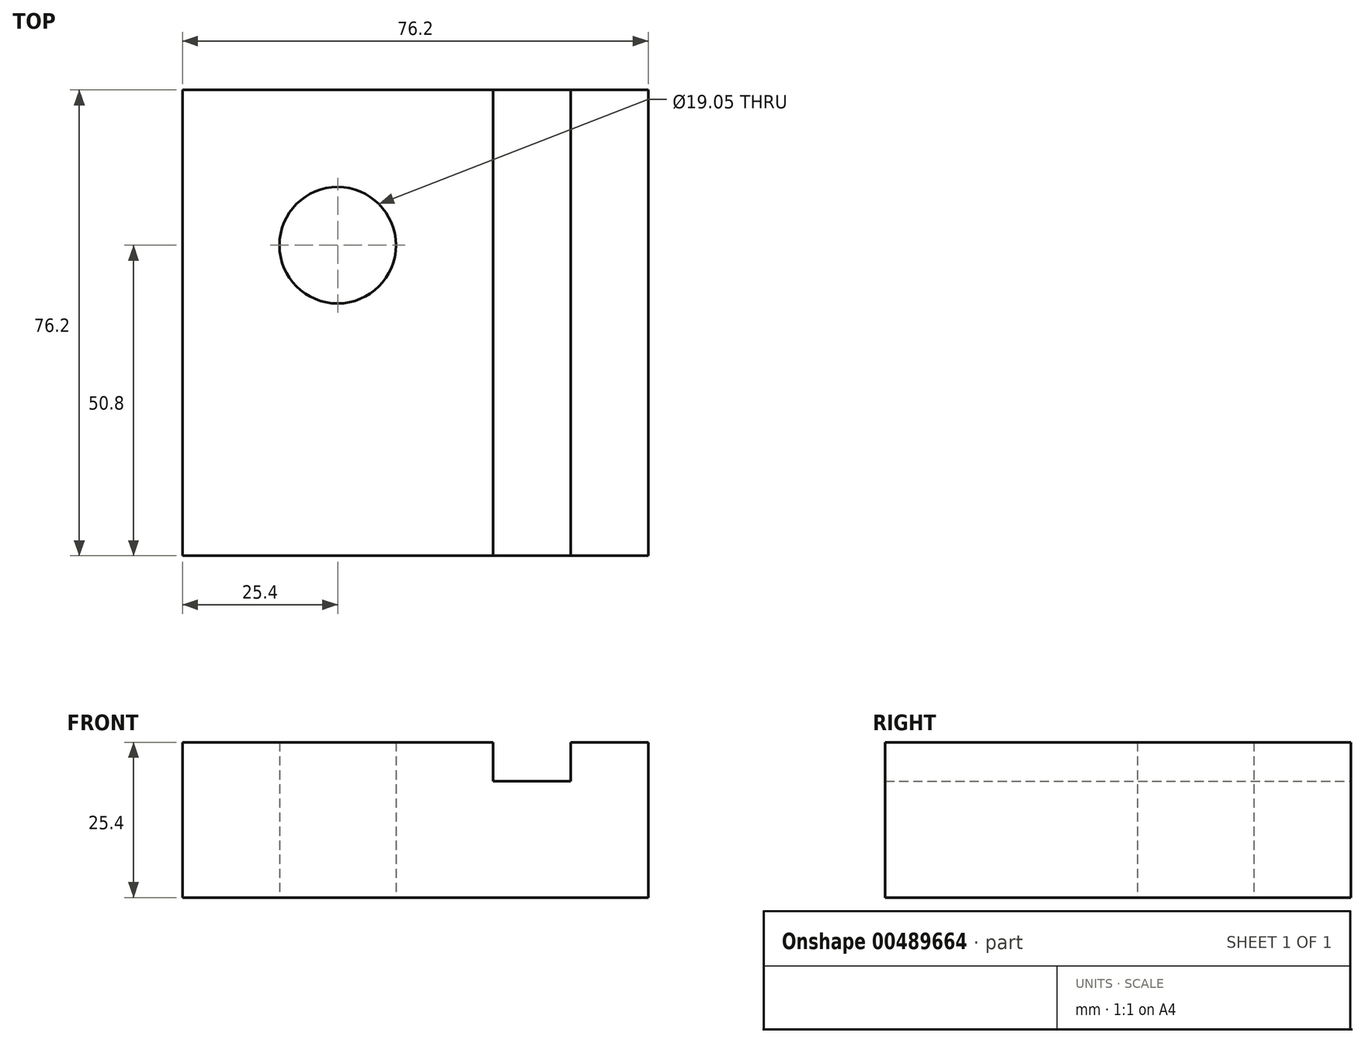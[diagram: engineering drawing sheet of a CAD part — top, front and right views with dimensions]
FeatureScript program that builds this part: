
annotation { "Feature Type Name" : "Feature", "Feature Type Description" : "" }
export const myFeature = defineFeature(function(context is Context, id is Id, definition is map)
    precondition{}
    {
        {
            var Q0;
            Q0=qCreatedBy(makeId("Front.planeOp"),FACE);
            var sketch = newSketch(context, id + "F0", { "sketchPlane" : qUnion([Q0])});
            skLineSegment(sketch, "E0", {"start": v(25.4, 0) * mm, "end": v(-50.8, 0) * mm});
            skLineSegment(sketch, "E1", {"start": v(-50.8, 0) * mm, "end": v(-50.8, 25.4) * mm});
            skLineSegment(sketch, "E2", {"start": v(-50.8, 25.4) * mm, "end": v(0, 25.4) * mm});
            skLineSegment(sketch, "E3", {"start": v(0, 25.4) * mm, "end": v(0, 19.05) * mm});
            skLineSegment(sketch, "E4", {"start": v(0, 19.05) * mm, "end": v(12.7, 19.05) * mm});
            skLineSegment(sketch, "E5", {"start": v(12.7, 19.05) * mm, "end": v(12.7, 25.4) * mm});
            skLineSegment(sketch, "E6", {"start": v(12.7, 25.4) * mm, "end": v(25.4, 25.4) * mm});
            skLineSegment(sketch, "E7", {"start": v(25.4, 25.4) * mm, "end": v(25.4, 0) * mm});
            skSolve(sketch);
        }
        {
            var Q0;
            Q0=makeQuery(id+"F0.imprint","IMPRINT",FACE,{"disambiguationData":[TD([[makeQuery(id+"F0.imprint","IMPRINT",EDGE,{"derivedFrom":sQuery(id+"F0.wireOp",EDGE,"E0")}),-1.0]])]});
            extrude(context, id + "F1", {"entities" : qUnion([Q0]), "depth" : 76.2 * mm});
        }
        {
            var Q0;
            Q0=qCreatedBy(makeId("Top.planeOp"),FACE);
            var sketch = newSketch(context, id + "F2", { "sketchPlane" : qUnion([Q0])});
            skCircle(sketch, "E8", {"center": v(-25.4, -25.4) * mm, "radius": 9.52 * mm});
            skSolve(sketch);
        }
        {
            var Q0;
            Q0 = qSketchRegion(id + "F2", true);
            extrude(context, id + "F3", {"entities" : qUnion([Q0]), "operationType" : NewBodyOperationType.REMOVE, "depth" : 76.2 * mm, "offsetDistance" : 25.4 * mm});
        }
    });
